# Revit family: NAU_Naughtone_Stng_Always_Stool
name_source: partatom
category: Generic Models
revit_build: Autodesk Revit 2018 (Build: 20170223_1515(x64)
units: mm (PartAtom-declared; Revit-internal decimal feet)

## family parameters
Always vertical = Yes
Can host rebar = No
Cut with Voids When Loaded = No
OmniClass Number = 23.40.00.00
OmniClass Title = Equipment and Furnishings
Part Type = Normal
Room Calculation Point = No
Round Connector Dimension = Use Diameter
Shared = No
Work Plane-Based = No

## types (2) — shared parameters
Assembly Code = E2020200
AssetType = Movable
BIMObjectName = NAU_Naughtone_Seating_Always_Stool
Category = Pr_40_50_12 : Chairs, seats and benches
Color = Various
DurationUnit = year
IfcExportAs = IfcFurnishingElementType
IfcExportType = STOOL
Keynote = Pr_40_50_12
MainColor = Various
ManufacturerAddress = Knaresborough Tech Park, Manse Lane, Knaresborough, HG5 8LF
ManufacturerName = Naughtone
ManufacturerURL = www.naughtone.com
NBSDescription = Seating
NBSReference = 45-35-72/352
Name = Seating_Always_Stool_Naughtone
NominalLength = 630 mm
NominalWidth = 600 mm
ProductInformation = www.naughtone.com/products/always/
ReplacementCost = 0.00
Revision = 2
Shape = Rectangular
SustainabilityPerformance = FISP certified. ISO 14001. SCS indoor advantage gold
URL = www.naughtone.com
Uniclass2015Code = Pr_40_50_12
Uniclass2015Title = Chairs, seats and benches
Version = 1
WarrantyDescription = Request warranty information from naughtone
WarrantyDurationLabor = 7
WarrantyDurationParts = 7
WarrantyDurationUnit = year

## per-type parameters (varying)
| type | Description | HighestSeatingHeight | IsBarHeight | IsCounterHeight | LowestSeatingHeight | Model | ModelNumber | ModelReference | NominalHeight | SeatingHeight | Size |
| ALCHSST4 - Always Counter Height Stool on 4 Leg Base | Always Counter Height Stool on 4 Leg Base | 655 mm | No | Yes | 655 mm | ALCHSST4 | ALCHSST4 | Always Counter Height Stool on 4 Leg Base | 965 mm | 655 mm | 630 x 600 x 965mm |
| ALBSST4 - Always Barstool on 4 Leg Base | Always Barstool on 4 Leg Base | 755 mm | Yes | No | 755 mm | ALBSST4 | ALBSST4 | Always Barstool on 4 Leg Base | 1065 mm  [stored 3.49409 ft] | 755 mm | 630 x 600 x 1065mm |

note: [stored X ft] marks values corroborated as IEEE doubles in the binary element streams (Revit-internal decimal feet)

## geometry (parser evidence)
native form markers: Blend x2, Sweep x2
no freeform markers — native parametric forms only
